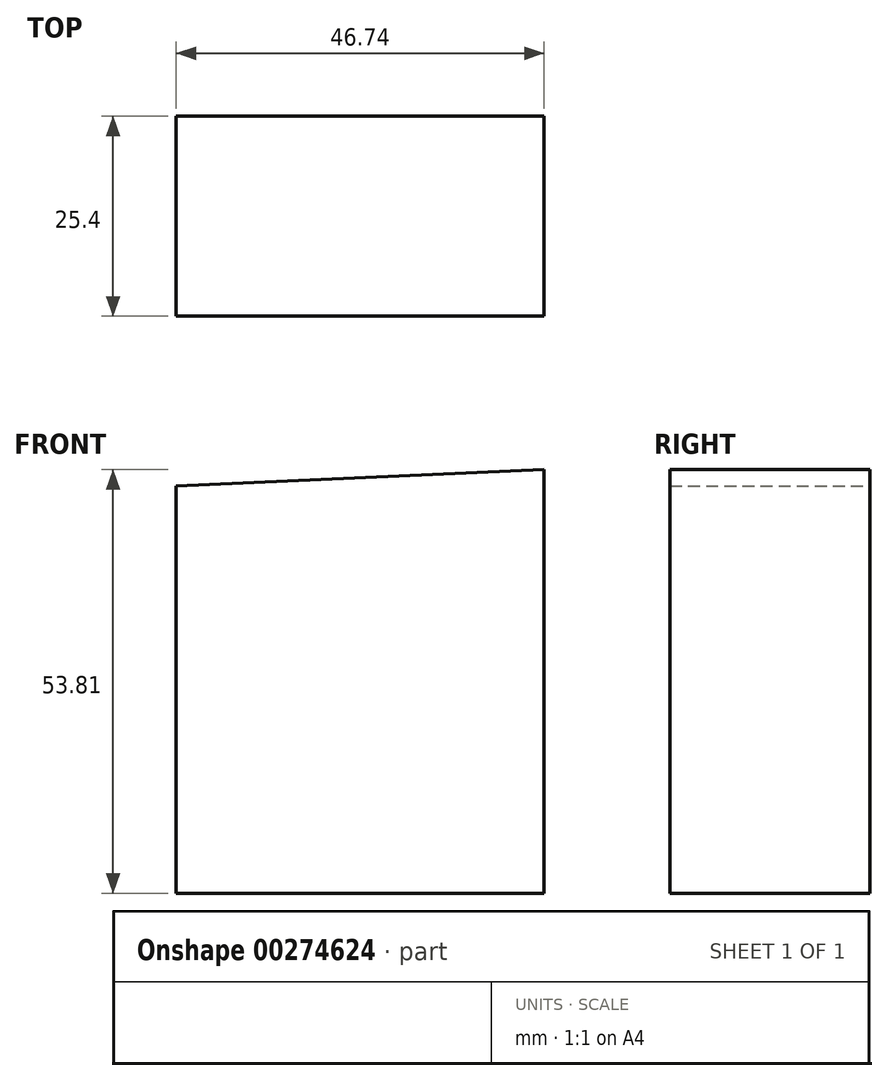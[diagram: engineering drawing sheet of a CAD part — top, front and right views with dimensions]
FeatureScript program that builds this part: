
annotation { "Feature Type Name" : "Feature", "Feature Type Description" : "" }
export const myFeature = defineFeature(function(context is Context, id is Id, definition is map)
    precondition{}
    {
        {
            var Q0;
            Q0=qCreatedBy(makeId("Front.planeOp"),FACE);
            var sketch = newSketch(context, id + "F0", { "sketchPlane" : qUnion([Q0])});
            skLineSegment(sketch, "E0", {"start": v(-60.31, 51.74) * mm, "end": v(-60.31, 0) * mm});
            skLineSegment(sketch, "E1", {"start": v(-13.57, 0) * mm, "end": v(-13.57, 53.81) * mm});
            skLineSegment(sketch, "E2", {"start": v(-13.57, 53.81) * mm, "end": v(-60.31, 51.74) * mm});
            skLineSegment(sketch, "E3", {"start": v(-60.31, 0) * mm, "end": v(-13.57, 0) * mm});
            skSolve(sketch);
        }
        {
            var Q0;
            Q0 = qSketchRegion(id + "F0", true);
            extrude(context, id + "F1", {"entities" : qUnion([Q0]), "depth" : 25.4 * mm});
        }
    });
